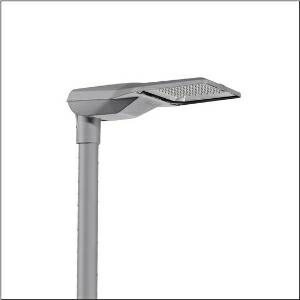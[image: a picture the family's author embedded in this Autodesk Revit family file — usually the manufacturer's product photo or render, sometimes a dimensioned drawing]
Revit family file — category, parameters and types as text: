
# Revit family: streetlight_sl_21_iq_midi___st0_8a_5xe3c61g08nb_b7e9
name_source: partatom
category: Lighting Fixtures
units: mm (PartAtom-declared; Revit-internal decimal feet)

## family parameters
Cut with Voids When Loaded = No
Host = Face
Light Source = No
Part Type = Normal
Room Calculation Point = No
Round Connector Dimension = Use Diameter
Shared = No

## types (1)
- --- (1 x LED, 20820 lm, 155.5 W, 2700K)
    Apparent Load = 155 VA
    CIE Flux Codes = 41 75 97 100 100
    Color Rendering = 70
    Color Temperature = 2700K
    Default Elevation = 1800 mm
    Description = Streetlight SL 21 iQ midi, mast luminaire, primary light control with lens, of PMMA, primary optical cover: cover, of toughened safety glass, transparent, light distribution: ST0.8a, light emission: direct distribution, primary light characteristic: asymmetric, installation type: post-top, side-entry, LED, High Power LED, rated luminous flux: 20.820lm, luminous efficacy: 134lm/W, light colour: 727, colour temperature: 2700K, control gear: iQ Street-Remote, control: Street-Remote, Auto-Match, Temp-Guard, Lumen-Switch, Night-Set, Smart-Wire, Light-Fading, Desk-Remote (wireless, voltage-free reading and setting of iQ features in the workshop via application-optimized NFC function/RFID function), optimised constant luminous flux control (CLO 2.0), pre-setting: linear dimming characteristic, mains connection: 230..240V, AC, 50/60Hz, start of lifetime: 156W, end of service life: 162W, reduction: 69W, luminaire housing, of diecast aluminium, powder-coated, SITECO metallic grey (DB 702S), corrosivity category C5 high according to DIN EN ISO 12944, please order mast flange separately, inclination adjustable: 0°, 5°, 10°, 15°, sealing non-destructively replaceable, multi-level sealing system, length: 644mm, width: 335mm, height: 110mm, mast flange for spigot size: 42mm (side-entry): 5XC10008XM4, 60/48mm (side-entry/post-top): 5XC10108XM2, 76/60mm (side-entry/post-top): 5XC10108XM1, mounting height: 4..8m, protection rating (complete): IP66, insulation class (complete): insulation class II (safety insulation), certification: CE, ENEC, ENEC+, VDE, impact resistance: IK10, permissible operating ambient temperature for outdoor applications: -40..+50°C, standard-compliant lighting for roads and squares, packaging unit: 1 piece

Light Distribution: ST0.8a
    Height = 111 mm
    Lamp = 1 x LED
    Lamp Light Flux = 20820 lm
    Lamp Power = 155.5 W
    Lamp count = 1
    Length = 644 mm
    Luminous efficacy = 134 lm/W
    Manufacturer = Siteco
    ModVariant = No
    Model = 5XE3C61G08NB
    Number of Poles = 1
    OnlyDefault = Yes
    Power Factor = 1
    Product Name = Streetlight SL 21 iQ midi | ST0.8a
    Product group = mast luminaire | pylon top
    ProductGroupID = 6100
    Protection Class = Protection class II
    Protection Degree = IP 66
    RLX_Detail_Level = 1
    RLX_Emergency_Light_Flux = 0 lm
    RLX_Emergency_Type = 0
    RLX_Emergency_Type_DB = No
    RlxData = <blob elided: 27189 chars, md5=d90acaab>
    Socket = socket
    Standby Power = 0 W
    System Light Flux = 20820 lm
    System Power = 155 W
    Type Comments = factory setting: luminous flux: 100 % | dim-lin: 254 | 823 mA
    Type Image = l_1004298.jpg
    URL = http://relux.com
    VarID = @adj_168273
    Voltage = 0 V
    Weight = 0.00 kg
    Width = 336 mm

## geometry (parser evidence)
native form markers: Blend x4, Sweep x12
no freeform markers — native parametric forms only
